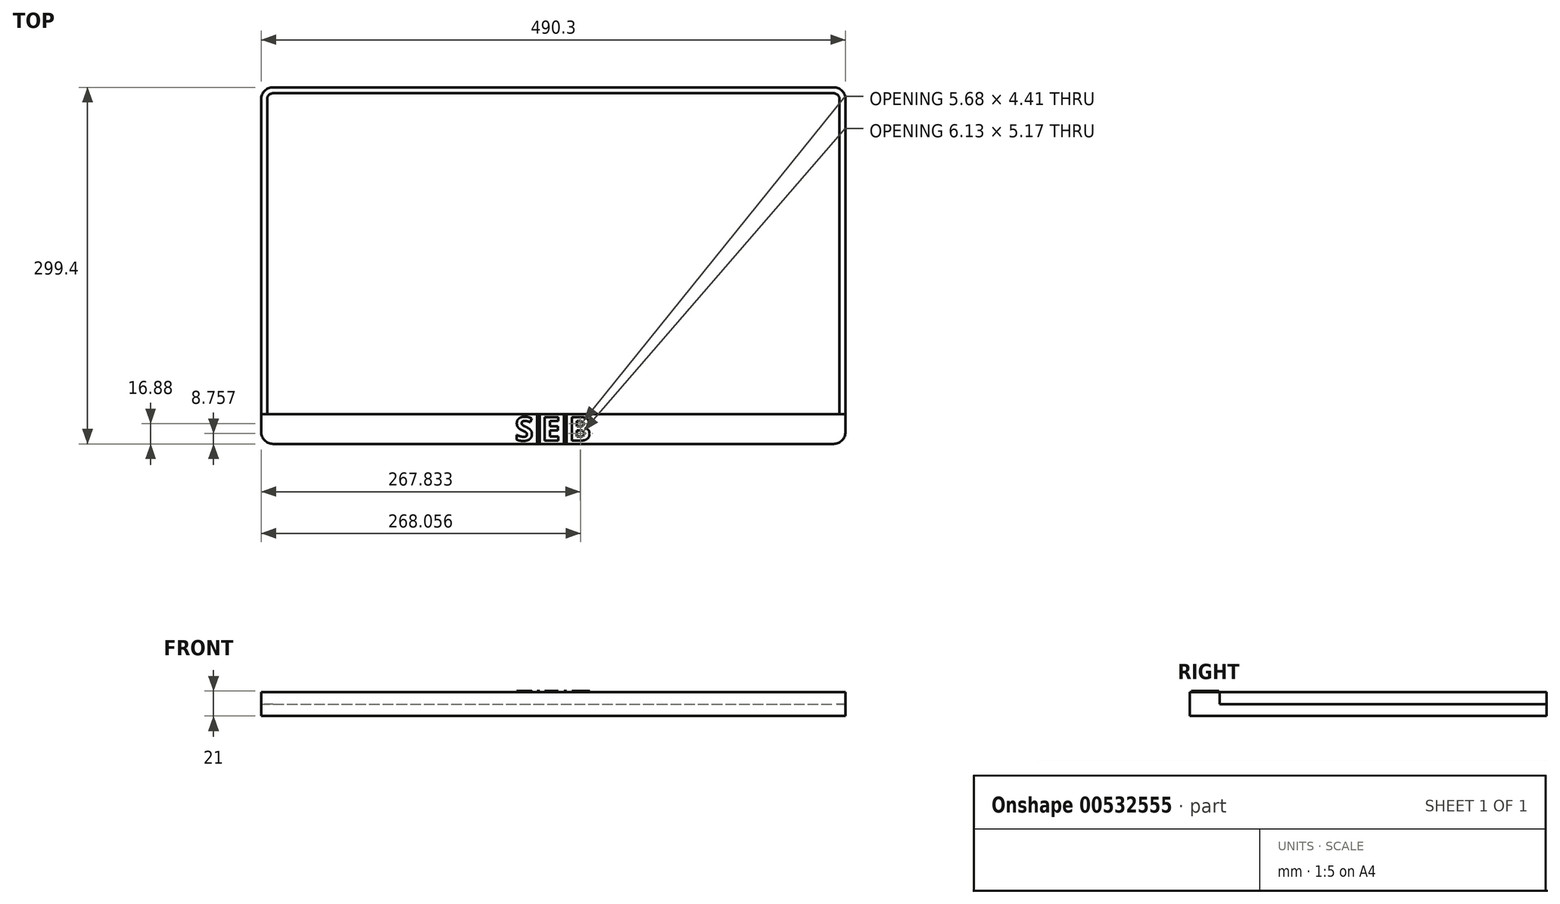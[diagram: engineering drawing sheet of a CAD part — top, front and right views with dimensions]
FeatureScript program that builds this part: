
annotation { "Feature Type Name" : "Feature", "Feature Type Description" : "" }
export const myFeature = defineFeature(function(context is Context, id is Id, definition is map)
    precondition{}
    {
        {
            var Q0;
            Q0=qCreatedBy(makeId("Top.planeOp"),FACE);
            var sketch = newSketch(context, id + "F0", { "sketchPlane" : qUnion([Q0])});
            skLineSegment(sketch, "E0.bottom", {"start": v(-235.15, 149.7) * mm, "end": v(235.15, 149.7) * mm});
            skLineSegment(sketch, "E0.top", {"start": v(-235.15, -149.7) * mm, "end": v(235.15, -149.7) * mm});
            skLineSegment(sketch, "E0.left", {"start": v(-245.15, 139.7) * mm, "end": v(-245.15, -139.7) * mm});
            skLineSegment(sketch, "E0.right", {"start": v(245.15, 139.7) * mm, "end": v(245.15, -139.7) * mm});
            skPoint(sketch, "E0.middle", {"position": v(0, 0) * mm});
            skPoint(sketch, "E1.visualSharp", {"position": v(245.15, 149.7) * mm});
            skArc(sketch, "E1.filletArc", {"start": v(245.15, 139.7) * mm, "mid": v(242.22, 146.77) * mm, "end": v(235.15, 149.7) * mm});
            skPoint(sketch, "E2.visualSharp", {"position": v(245.15, -149.7) * mm});
            skArc(sketch, "E2.filletArc", {"start": v(235.15, -149.7) * mm, "mid": v(242.22, -146.77) * mm, "end": v(245.15, -139.7) * mm});
            skPoint(sketch, "E3.visualSharp", {"position": v(-245.15, -149.7) * mm});
            skArc(sketch, "E3.filletArc", {"start": v(-245.15, -139.7) * mm, "mid": v(-242.22, -146.77) * mm, "end": v(-235.15, -149.7) * mm});
            skPoint(sketch, "E4.visualSharp", {"position": v(-245.15, 149.7) * mm});
            skArc(sketch, "E4.filletArc", {"start": v(-235.15, 149.7) * mm, "mid": v(-242.22, 146.77) * mm, "end": v(-245.15, 139.7) * mm});
            skSolve(sketch);
        }
        {
            var Q0;
            Q0 = qSketchRegion(id + "F0", true);
            extrude(context, id + "F1", {"entities" : qUnion([Q0]), "depth" : 20 * mm, "offsetDistance" : 25 * mm});
        }
        {
            var Q0;
            Q0=makeQuery(id+"F1.opExtrude","CAP_FACE",FACE,{"disambiguationData":[OSD([sQuery(id+"F0.wireOp",EDGE,"E0.bottom"),sQuery(id+"F0.wireOp",EDGE,"E0.top"),sQuery(id+"F0.wireOp",EDGE,"E0.left"),sQuery(id+"F0.wireOp",EDGE,"E0.right"),sQuery(id+"F0.wireOp",EDGE,"E1.filletArc"),sQuery(id+"F0.wireOp",EDGE,"E2.filletArc"),sQuery(id+"F0.wireOp",EDGE,"E3.filletArc"),sQuery(id+"F0.wireOp",EDGE,"E4.filletArc")])],"isStart":false});
            var sketch = newSketch(context, id + "F2", { "sketchPlane" : qUnion([Q0])});
            skLineSegment(sketch, "E5.bottom", {"start": v(-245.15, -124.7) * mm, "end": v(245.15, -124.7) * mm});
            skLineSegment(sketch, "E5.top", {"start": v(-235.15, 149.7) * mm, "end": v(235.15, 149.7) * mm});
            skLineSegment(sketch, "E5.left", {"start": v(-245.15, -124.7) * mm, "end": v(-245.15, 139.7) * mm});
            skLineSegment(sketch, "E5.right", {"start": v(245.15, -124.7) * mm, "end": v(245.15, 139.7) * mm});
            skPoint(sketch, "E6.visualSharp", {"position": v(245.15, 149.7) * mm});
            skArc(sketch, "E6.filletArc", {"start": v(245.15, 139.7) * mm, "mid": v(242.22, 146.77) * mm, "end": v(235.15, 149.7) * mm});
            skPoint(sketch, "E7.visualSharp", {"position": v(-245.15, 149.7) * mm});
            skArc(sketch, "E7.filletArc", {"start": v(-235.15, 149.7) * mm, "mid": v(-242.22, 146.77) * mm, "end": v(-245.15, 139.7) * mm});
            skSolve(sketch);
        }
        {
            var Q0;
            Q0 = qSketchRegion(id + "F2", true);
            extrude(context, id + "F3", {"entities" : qUnion([Q0]), "operationType" : NewBodyOperationType.REMOVE, "oppositeDirection" : true, "depth" : 10 * mm, "offsetDistance" : 25 * mm});
        }
        {
            var Q0;
            Q0=makeQuery(id+"F3.boolean.opBoolean","COPY",FACE,{"derivedFrom":makeQuery(id+"F3.opExtrude","CAP_FACE",FACE,{"disambiguationData":[OSD([sQuery(id+"F2.wireOp",EDGE,"E5.bottom"),sQuery(id+"F2.wireOp",EDGE,"E5.top"),sQuery(id+"F2.wireOp",EDGE,"E5.left"),sQuery(id+"F2.wireOp",EDGE,"E5.right"),sQuery(id+"F2.wireOp",EDGE,"E6.filletArc"),sQuery(id+"F2.wireOp",EDGE,"E7.filletArc")])],"isStart":false})});
            var sketch = newSketch(context, id + "F4", { "sketchPlane" : qUnion([Q0])});
            skLineSegment(sketch, "E8.bottom", {"start": v(245.15, -124.7) * mm, "end": v(-245.15, -124.7) * mm});
            skLineSegment(sketch, "E8.top", {"start": v(235.15, 149.7) * mm, "end": v(-235.15, 149.7) * mm});
            skLineSegment(sketch, "E8.left", {"start": v(245.15, -124.7) * mm, "end": v(245.15, 139.7) * mm});
            skLineSegment(sketch, "E8.right", {"start": v(-245.15, -124.7) * mm, "end": v(-245.15, 139.7) * mm});
            skPoint(sketch, "E9.visualSharp", {"position": v(-245.15, 149.7) * mm});
            skArc(sketch, "E9.filletArc", {"start": v(-235.15, 149.7) * mm, "mid": v(-242.22, 146.77) * mm, "end": v(-245.15, 139.7) * mm});
            skPoint(sketch, "E10.visualSharp", {"position": v(245.15, 149.7) * mm});
            skArc(sketch, "E10.filletArc", {"start": v(245.15, 139.7) * mm, "mid": v(242.22, 146.77) * mm, "end": v(235.15, 149.7) * mm});
            skSolve(sketch);
        }
        {
            var Q0;
            Q0 = qSketchRegion(id + "F4", true);
            extrude(context, id + "F5", {"entities" : qUnion([Q0]), "depth" : 10 * mm, "offsetDistance" : 25 * mm});
        }
        {
            var Q0;
            Q0=makeQuery(id+"F5.opExtrude","CAP_FACE",FACE,{"disambiguationData":[OSD([sQuery(id+"F4.wireOp",EDGE,"E8.bottom"),sQuery(id+"F4.wireOp",EDGE,"E8.top"),sQuery(id+"F4.wireOp",EDGE,"E8.left"),sQuery(id+"F4.wireOp",EDGE,"E8.right"),sQuery(id+"F4.wireOp",EDGE,"E9.filletArc"),sQuery(id+"F4.wireOp",EDGE,"E10.filletArc")])],"isStart":false});
            var sketch = newSketch(context, id + "F6", { "sketchPlane" : qUnion([Q0])});
            skLineSegment(sketch, "E11.bottom", {"start": v(240.15, -124.7) * mm, "end": v(-240.15, -124.7) * mm});
            skLineSegment(sketch, "E11.top", {"start": v(235.15, 144.7) * mm, "end": v(-235.15, 144.7) * mm});
            skLineSegment(sketch, "E11.left", {"start": v(240.15, -124.7) * mm, "end": v(240.15, 139.7) * mm});
            skLineSegment(sketch, "E11.right", {"start": v(-240.15, -124.7) * mm, "end": v(-240.15, 139.7) * mm});
            skPoint(sketch, "E12.visualSharp", {"position": v(-240.15, 144.7) * mm});
            skArc(sketch, "E12.filletArc", {"start": v(-235.15, 144.7) * mm, "mid": v(-238.69, 143.24) * mm, "end": v(-240.15, 139.7) * mm});
            skPoint(sketch, "E13.visualSharp", {"position": v(240.15, 144.7) * mm});
            skArc(sketch, "E13.filletArc", {"start": v(240.15, 139.7) * mm, "mid": v(238.69, 143.24) * mm, "end": v(235.15, 144.7) * mm});
            skSolve(sketch);
        }
        {
            var Q0;
            Q0 = qSketchRegion(id + "F6", true);
            extrude(context, id + "F7", {"entities" : qUnion([Q0]), "depth" : 0.1 * mm, "offsetDistance" : 25 * mm});
        }
        {
            var Q0;
            Q0=makeQuery(id+"F1.opExtrude","CAP_FACE",FACE,{"disambiguationData":[OSD([sQuery(id+"F0.wireOp",EDGE,"E0.bottom"),sQuery(id+"F0.wireOp",EDGE,"E0.top"),sQuery(id+"F0.wireOp",EDGE,"E0.left"),sQuery(id+"F0.wireOp",EDGE,"E0.right"),sQuery(id+"F0.wireOp",EDGE,"E1.filletArc"),sQuery(id+"F0.wireOp",EDGE,"E2.filletArc"),sQuery(id+"F0.wireOp",EDGE,"E3.filletArc"),sQuery(id+"F0.wireOp",EDGE,"E4.filletArc")])],"isStart":false});
            var sketch = newSketch(context, id + "F8", { "sketchPlane" : qUnion([Q0])});
            skText(sketch, "E14", { "text": "S E B", "fontName": "OpenSans-Bold.ttf"});
            skLineSegment(sketch, "E15.bottom", {"start": v(-13.5, -125.37) * mm, "end": v(-11.5, -125.37) * mm});
            skLineSegment(sketch, "E15.top", {"start": v(-13.5, -148.63) * mm, "end": v(-11.5, -148.63) * mm});
            skLineSegment(sketch, "E15.left", {"start": v(-13.5, -125.37) * mm, "end": v(-13.5, -148.63) * mm});
            skLineSegment(sketch, "E15.right", {"start": v(-11.5, -125.37) * mm, "end": v(-11.5, -148.63) * mm});
            skPoint(sketch, "E15.middle", {"position": v(-12.5, -137) * mm});
            skPoint(sketch, "E15.middle.positionSnap0", {"position": v(-32.15, -137) * mm});
            skPoint(sketch, "E15.centerSnap0", {"position": v(-32.15, -137) * mm});
            skLineSegment(sketch, "E16.bottom", {"start": v(9, -125.37) * mm, "end": v(11, -125.37) * mm});
            skLineSegment(sketch, "E16.top", {"start": v(9, -148.63) * mm, "end": v(11, -148.63) * mm});
            skLineSegment(sketch, "E16.left", {"start": v(9, -125.37) * mm, "end": v(9, -148.63) * mm});
            skLineSegment(sketch, "E16.right", {"start": v(11, -125.37) * mm, "end": v(11, -148.63) * mm});
            skPoint(sketch, "E16.middle", {"position": v(10, -137) * mm});
            const initialGuessF8  = {"E14": [-0.03215, -0.147, 1, 0, 0.02]};
            skSetInitialGuess(sketch, initialGuessF8);
            skSolve(sketch);
        }
        {
            var Q0;
            Q0 = qSketchRegion(id + "F8", true);
            extrude(context, id + "F9", {"entities" : qUnion([Q0]), "depth" : 1 * mm, "offsetDistance" : 25 * mm});
        }
    });
